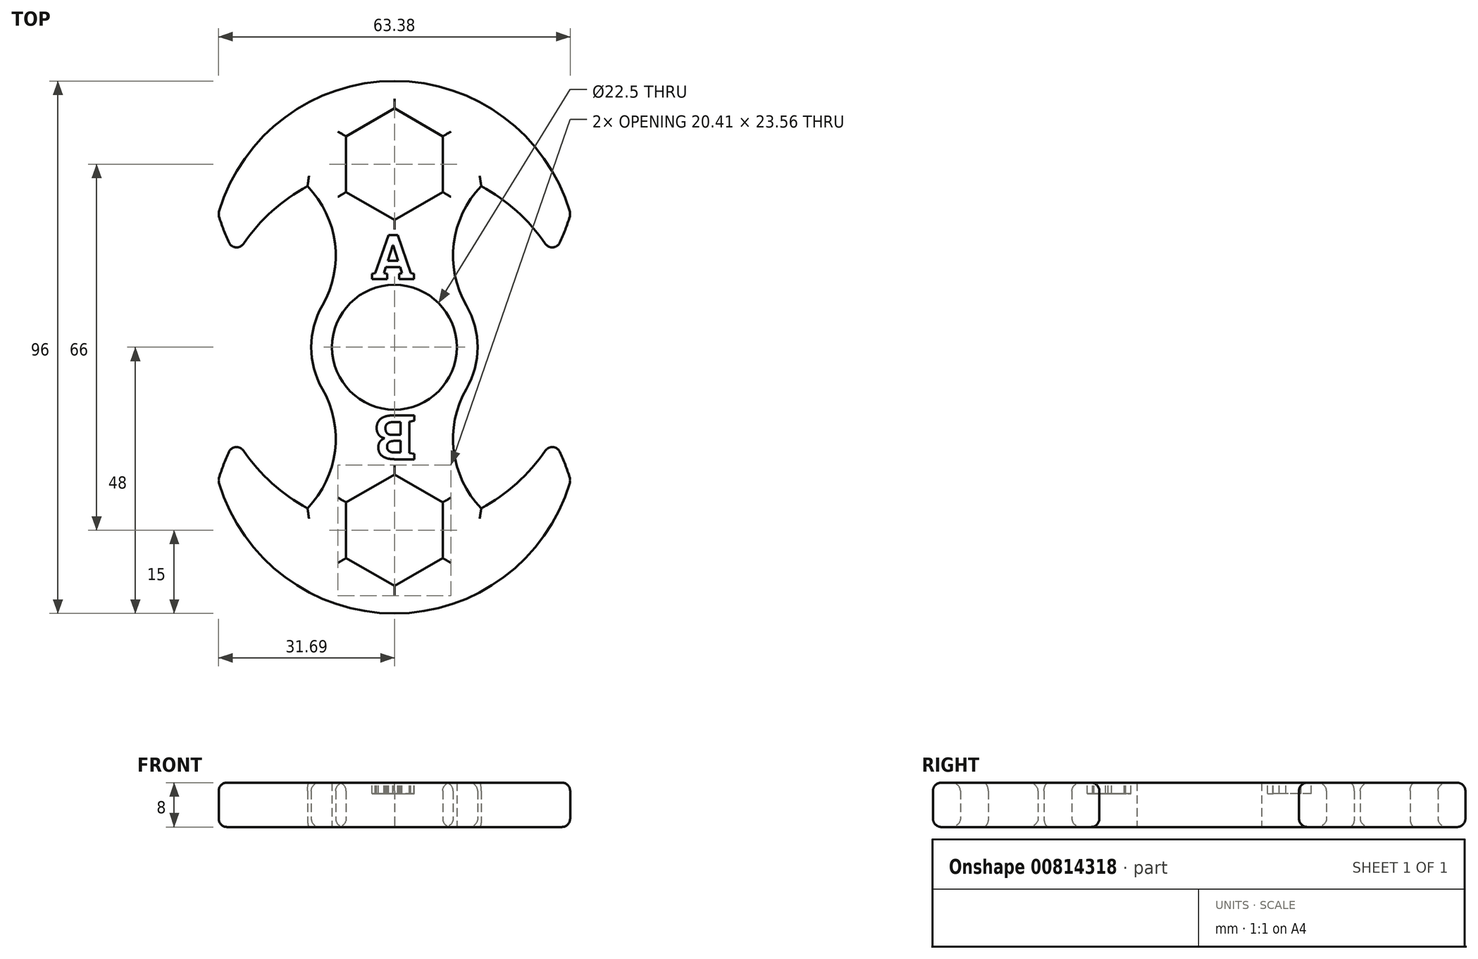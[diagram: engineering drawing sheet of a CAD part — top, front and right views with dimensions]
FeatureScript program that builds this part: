
annotation { "Feature Type Name" : "Feature", "Feature Type Description" : "" }
export const myFeature = defineFeature(function(context is Context, id is Id, definition is map)
    precondition{}
    {
        {
            var Q0;
            Q0=qCreatedBy(makeId("Top.planeOp"),FACE);
            var sketch = newSketch(context, id + "F0", { "sketchPlane" : qUnion([Q0])});
            skCircle(sketch, "E0", {"center": v(0, 0) * mm, "radius": 11.25 * mm});
            skArc(sketch, "E1", {"start": v(13, -7.5) * mm, "mid": v(15, 0) * mm, "end": v(13, 7.5) * mm});
            skCircle(sketch, "E2", {"center": v(0, 33) * mm, "radius": 10.05 * mm});
            skPoint(sketch, "E3.orphan", {"position": v(0, -30.51) * mm});
            skCircle(sketch, "E4", {"center": v(0, -33) * mm, "radius": 10.05 * mm});
            skArc(sketch, "E5", {"start": v(31.75, -24) * mm, "mid": v(30.4, -20.15) * mm, "end": v(28.58, -16.5) * mm});
            skArc(sketch, "E6", {"start": v(28.58, 16.5) * mm, "mid": v(30.4, 20.15) * mm, "end": v(31.75, 24) * mm});
            skArc(sketch, "E7", {"start": v(-28.58, -16.5) * mm, "mid": v(-23, -23.67) * mm, "end": v(-15.67, -29.04) * mm});
            skArc(sketch, "E8", {"start": v(31.75, 24) * mm, "mid": v(0, 48) * mm, "end": v(-31.75, 24) * mm});
            skArc(sketch, "E9", {"start": v(-31.75, -24) * mm, "mid": v(0, -48) * mm, "end": v(31.75, -24) * mm});
            skArc(sketch, "E10.trimOffspring", {"start": v(-28.58, -16.5) * mm, "mid": v(-30.4, -20.15) * mm, "end": v(-31.75, -24) * mm});
            skArc(sketch, "E11.trimOffspring", {"start": v(15.67, -29.04) * mm, "mid": v(23, -23.67) * mm, "end": v(28.58, -16.5) * mm});
            skArc(sketch, "E12.trimOffspring", {"start": v(-31.75, 24) * mm, "mid": v(-30.4, 20.15) * mm, "end": v(-28.58, 16.5) * mm});
            skArc(sketch, "E13.trimOffspring", {"start": v(28.58, 16.5) * mm, "mid": v(23, 23.67) * mm, "end": v(15.67, 29.04) * mm});
            skArc(sketch, "E14", {"start": v(15.67, 29.04) * mm, "mid": v(10.72, 18.72) * mm, "end": v(13, 7.5) * mm});
            skArc(sketch, "E15", {"start": v(13, -7.5) * mm, "mid": v(10.72, -18.72) * mm, "end": v(15.67, -29.04) * mm});
            skArc(sketch, "E16", {"start": v(-15.67, -29.04) * mm, "mid": v(-10.72, -18.72) * mm, "end": v(-13, -7.5) * mm});
            skArc(sketch, "E17.trimOffspring", {"start": v(-13, 7.5) * mm, "mid": v(-10.72, 18.72) * mm, "end": v(-15.67, 29.04) * mm});
            skArc(sketch, "E18.trimOffspring", {"start": v(-15.67, 29.04) * mm, "mid": v(-23, 23.67) * mm, "end": v(-28.58, 16.5) * mm});
            skArc(sketch, "E19.trimOffspring", {"start": v(-13, 7.5) * mm, "mid": v(-15, 0) * mm, "end": v(-13, -7.5) * mm});
            skCircle(sketch, "E20.cCircle", {"center": v(0, 33) * mm, "radius": 10.05 * mm, "construction": true});
            skLineSegment(sketch, "E20.0", {"start": v(0, 22.95) * mm, "end": v(-8.7, 27.98) * mm});
            skLineSegment(sketch, "E20.1", {"start": v(-8.7, 27.98) * mm, "end": v(-8.7, 38.03) * mm});
            skLineSegment(sketch, "E20.2", {"start": v(-8.7, 38.03) * mm, "end": v(0, 43.05) * mm});
            skLineSegment(sketch, "E20.3", {"start": v(0, 43.05) * mm, "end": v(8.7, 38.02) * mm});
            skLineSegment(sketch, "E20.4", {"start": v(8.7, 38.03) * mm, "end": v(8.7, 27.98) * mm});
            skLineSegment(sketch, "E20.5", {"start": v(8.7, 27.98) * mm, "end": v(0, 22.95) * mm});
            skCircle(sketch, "E21.cCircle", {"center": v(0, -33) * mm, "radius": 10.05 * mm, "construction": true});
            skLineSegment(sketch, "E21.0", {"start": v(0, -22.95) * mm, "end": v(8.7, -27.98) * mm});
            skLineSegment(sketch, "E21.1", {"start": v(8.7, -27.98) * mm, "end": v(8.7, -38.03) * mm});
            skLineSegment(sketch, "E21.2", {"start": v(8.7, -38.03) * mm, "end": v(0, -43.05) * mm});
            skLineSegment(sketch, "E21.3", {"start": v(0, -43.05) * mm, "end": v(-8.7, -38.03) * mm});
            skLineSegment(sketch, "E21.4", {"start": v(-8.7, -38.03) * mm, "end": v(-8.7, -27.97) * mm});
            skLineSegment(sketch, "E21.5", {"start": v(-8.7, -27.97) * mm, "end": v(0, -22.95) * mm});
            skSolve(sketch);
        }
        {
            var Q0;
            {var subQ0=sQuery(id+"F0.wireOp",EDGE,"E20.0");Q0=makeQuery(id+"F0.imprint","IMPRINT",FACE,{"disambiguationData":[TD([[makeQuery(id+"F0.imprint","IMPRINT",EDGE,{"derivedFrom":subQ0}),1.0]])]});}
            var Q1;
            {var subQ0=sQuery(id+"F0.wireOp",EDGE,"E20.5");Q1=makeQuery(id+"F0.imprint","IMPRINT",FACE,{"disambiguationData":[TD([[makeQuery(id+"F0.imprint","IMPRINT",EDGE,{"derivedFrom":subQ0}),1.0]])]});}
            var Q2;
            {var subQ0=sQuery(id+"F0.wireOp",EDGE,"E20.4");Q2=makeQuery(id+"F0.imprint","IMPRINT",FACE,{"disambiguationData":[TD([[makeQuery(id+"F0.imprint","IMPRINT",EDGE,{"derivedFrom":subQ0}),1.0]])]});}
            var Q3;
            {var subQ0=sQuery(id+"F0.wireOp",EDGE,"E20.2");Q3=makeQuery(id+"F0.imprint","IMPRINT",FACE,{"disambiguationData":[TD([[makeQuery(id+"F0.imprint","IMPRINT",EDGE,{"derivedFrom":subQ0}),1.0]])]});}
            var Q4;
            {var subQ0=sQuery(id+"F0.wireOp",EDGE,"E20.3");Q4=makeQuery(id+"F0.imprint","IMPRINT",FACE,{"disambiguationData":[TD([[makeQuery(id+"F0.imprint","IMPRINT",EDGE,{"derivedFrom":subQ0}),1.0]])]});}
            var Q5;
            {var subQ0=sQuery(id+"F0.wireOp",EDGE,"E20.1");Q5=makeQuery(id+"F0.imprint","IMPRINT",FACE,{"disambiguationData":[TD([[makeQuery(id+"F0.imprint","IMPRINT",EDGE,{"derivedFrom":subQ0}),1.0]])]});}
            var Q6;
            {var subQ0=sQuery(id+"F0.wireOp",EDGE,"E21.0");Q6=makeQuery(id+"F0.imprint","IMPRINT",FACE,{"disambiguationData":[TD([[makeQuery(id+"F0.imprint","IMPRINT",EDGE,{"derivedFrom":subQ0}),1.0]])]});}
            var Q7;
            {var subQ0=sQuery(id+"F0.wireOp",EDGE,"E21.1");Q7=makeQuery(id+"F0.imprint","IMPRINT",FACE,{"disambiguationData":[TD([[makeQuery(id+"F0.imprint","IMPRINT",EDGE,{"derivedFrom":subQ0}),1.0]])]});}
            var Q8;
            {var subQ0=sQuery(id+"F0.wireOp",EDGE,"E21.2");Q8=makeQuery(id+"F0.imprint","IMPRINT",FACE,{"disambiguationData":[TD([[makeQuery(id+"F0.imprint","IMPRINT",EDGE,{"derivedFrom":subQ0}),1.0]])]});}
            var Q9;
            Q9=makeQuery(id+"F0.imprint","IMPRINT",FACE,{"disambiguationData":[TD([[makeQuery(id+"F0.imprint","IMPRINT",EDGE,{"derivedFrom":sQuery(id+"F0.wireOp",EDGE,"E0")}),-1.0]])]});
            var Q10;
            {var subQ0=sQuery(id+"F0.wireOp",EDGE,"E21.3");Q10=makeQuery(id+"F0.imprint","IMPRINT",FACE,{"disambiguationData":[TD([[makeQuery(id+"F0.imprint","IMPRINT",EDGE,{"derivedFrom":subQ0}),1.0]])]});}
            var Q11;
            {var subQ0=sQuery(id+"F0.wireOp",EDGE,"E21.4");Q11=makeQuery(id+"F0.imprint","IMPRINT",FACE,{"disambiguationData":[TD([[makeQuery(id+"F0.imprint","IMPRINT",EDGE,{"derivedFrom":subQ0}),1.0]])]});}
            var Q12;
            {var subQ0=sQuery(id+"F0.wireOp",EDGE,"E21.5");Q12=makeQuery(id+"F0.imprint","IMPRINT",FACE,{"disambiguationData":[TD([[makeQuery(id+"F0.imprint","IMPRINT",EDGE,{"derivedFrom":subQ0}),1.0]])]});}
            var Q13;
            Q13=makeQuery(id+"F0.imprint","IMPRINT",FACE,{"disambiguationData":[TD([[makeQuery(id+"F0.imprint","IMPRINT",EDGE,{"derivedFrom":sQuery(id+"F0.wireOp",EDGE,"b09e6dd1-dab8-4b64-9b37-ad7a02245aec.sketch_text.stroke-16")}),1.0]])]});
            var Q14;
            Q14=makeQuery(id+"F0.imprint","IMPRINT",FACE,{"disambiguationData":[TD([[makeQuery(id+"F0.imprint","IMPRINT",EDGE,{"derivedFrom":sQuery(id+"F0.wireOp",EDGE,"b09e6dd1-dab8-4b64-9b37-ad7a02245aec.sketch_text.stroke-0")}),-1.0]])]});
            var Q15;
            Q15=makeQuery(id+"F0.imprint","IMPRINT",FACE,{"disambiguationData":[TD([[makeQuery(id+"F0.imprint","IMPRINT",EDGE,{"derivedFrom":sQuery(id+"F0.wireOp",EDGE,"b3a1ebe3-2c7f-47d1-8247-27ddfe72ac5a.sketch_text.stroke-23")}),1.0]])]});
            var Q16;
            Q16=makeQuery(id+"F0.imprint","IMPRINT",FACE,{"disambiguationData":[TD([[makeQuery(id+"F0.imprint","IMPRINT",EDGE,{"derivedFrom":sQuery(id+"F0.wireOp",EDGE,"b3a1ebe3-2c7f-47d1-8247-27ddfe72ac5a.sketch_text.stroke-16")}),1.0]])]});
            var Q17;
            Q17=makeQuery(id+"F0.imprint","IMPRINT",FACE,{"disambiguationData":[TD([[makeQuery(id+"F0.imprint","IMPRINT",EDGE,{"derivedFrom":sQuery(id+"F0.wireOp",EDGE,"b3a1ebe3-2c7f-47d1-8247-27ddfe72ac5a.sketch_text.stroke-0")}),-1.0]])]});
            extrude(context, id + "F1", {"entities" : qUnion([Q0, Q1, Q2, Q3, Q4, Q5, Q6, Q7, Q8, Q9, Q10, Q11, Q12, Q13, Q14, Q15, Q16, Q17]), "depth" : 8 * mm, "offsetDistance" : 25 * mm});
        }
        {
            var Q0;
            Q0=makeQuery(id+"F1.opExtrude","CAP_EDGE",EDGE,{"disambiguationData":[OSD([sQuery(id+"F0.wireOp",EDGE,"E8")])],"isStart":false});
            var Q1;
            Q1=makeQuery(id+"F1.opExtrude","CAP_EDGE",EDGE,{"disambiguationData":[OSD([sQuery(id+"F0.wireOp",EDGE,"E12.trimOffspring")])],"isStart":false});
            var Q2;
            Q2=makeQuery(id+"F1.opExtrude","CAP_EDGE",EDGE,{"disambiguationData":[OSD([sQuery(id+"F0.wireOp",EDGE,"E18.trimOffspring")])],"isStart":false});
            var Q3;
            Q3=makeQuery(id+"F1.opExtrude","CAP_EDGE",EDGE,{"disambiguationData":[OSD([sQuery(id+"F0.wireOp",EDGE,"E17.trimOffspring")])],"isStart":false});
            var Q4;
            Q4=makeQuery(id+"F1.opExtrude","CAP_EDGE",EDGE,{"disambiguationData":[OSD([sQuery(id+"F0.wireOp",EDGE,"E15")])],"isStart":false});
            var Q5;
            Q5=makeQuery(id+"F1.opExtrude","CAP_EDGE",EDGE,{"disambiguationData":[OSD([sQuery(id+"F0.wireOp",EDGE,"E13.trimOffspring")])],"isStart":false});
            var Q6;
            Q6=makeQuery(id+"F1.opExtrude","CAP_EDGE",EDGE,{"disambiguationData":[OSD([sQuery(id+"F0.wireOp",EDGE,"E6")])],"isStart":false});
            var Q7;
            Q7=makeQuery(id+"F1.opExtrude","CAP_EDGE",EDGE,{"disambiguationData":[OSD([sQuery(id+"F0.wireOp",EDGE,"E9")])],"isStart":false});
            var Q8;
            Q8=makeQuery(id+"F1.opExtrude","CAP_EDGE",EDGE,{"disambiguationData":[OSD([sQuery(id+"F0.wireOp",EDGE,"E5")])],"isStart":false});
            var Q9;
            Q9=makeQuery(id+"F1.opExtrude","CAP_EDGE",EDGE,{"disambiguationData":[OSD([sQuery(id+"F0.wireOp",EDGE,"E7")])],"isStart":false});
            var Q10;
            Q10=makeQuery(id+"F1.opExtrude","CAP_EDGE",EDGE,{"disambiguationData":[OSD([sQuery(id+"F0.wireOp",EDGE,"E10.trimOffspring")])],"isStart":false});
            var Q11;
            Q11=makeQuery(id+"F1.opExtrude","CAP_EDGE",EDGE,{"disambiguationData":[OSD([sQuery(id+"F0.wireOp",EDGE,"E11.trimOffspring")])],"isStart":false});
            var Q12;
            Q12=makeQuery(id+"F1.opExtrude","CAP_EDGE",EDGE,{"disambiguationData":[OSD([sQuery(id+"F0.wireOp",EDGE,"E9")])],"isStart":true});
            var Q13;
            Q13=makeQuery(id+"F1.opExtrude","CAP_EDGE",EDGE,{"disambiguationData":[OSD([sQuery(id+"F0.wireOp",EDGE,"E5")])],"isStart":true});
            var Q14;
            Q14=makeQuery(id+"F1.opExtrude","CAP_EDGE",EDGE,{"disambiguationData":[OSD([sQuery(id+"F0.wireOp",EDGE,"E11.trimOffspring")])],"isStart":true});
            var Q15;
            Q15=makeQuery(id+"F1.opExtrude","CAP_EDGE",EDGE,{"disambiguationData":[OSD([sQuery(id+"F0.wireOp",EDGE,"E15")])],"isStart":true});
            var Q16;
            Q16=makeQuery(id+"F1.opExtrude","CAP_EDGE",EDGE,{"disambiguationData":[OSD([sQuery(id+"F0.wireOp",EDGE,"E13.trimOffspring")])],"isStart":true});
            var Q17;
            Q17=makeQuery(id+"F1.opExtrude","CAP_EDGE",EDGE,{"disambiguationData":[OSD([sQuery(id+"F0.wireOp",EDGE,"E8")])],"isStart":true});
            var Q18;
            Q18=makeQuery(id+"F1.opExtrude","CAP_EDGE",EDGE,{"disambiguationData":[OSD([sQuery(id+"F0.wireOp",EDGE,"E12.trimOffspring")])],"isStart":true});
            var Q19;
            Q19=makeQuery(id+"F1.opExtrude","CAP_EDGE",EDGE,{"disambiguationData":[OSD([sQuery(id+"F0.wireOp",EDGE,"E17.trimOffspring")])],"isStart":true});
            var Q20;
            Q20=makeQuery(id+"F1.opExtrude","CAP_EDGE",EDGE,{"disambiguationData":[OSD([sQuery(id+"F0.wireOp",EDGE,"E10.trimOffspring")])],"isStart":true});
            var Q21;
            Q21=makeQuery(id+"F1.opExtrude","CAP_EDGE",EDGE,{"disambiguationData":[OSD([sQuery(id+"F0.wireOp",EDGE,"E7")])],"isStart":true});
            var Q22;
            Q22=makeQuery(id+"F1.opExtrude","CAP_EDGE",EDGE,{"disambiguationData":[OSD([sQuery(id+"F0.wireOp",EDGE,"E18.trimOffspring")])],"isStart":true});
            var Q23;
            Q23=makeQuery(id+"F1.opExtrude","SWEPT_EDGE",EDGE,{"disambiguationData":[OSD([sQuery(id+"F0.wireOp",EDGE,"E12.trimOffspring"),sQuery(id+"F0.wireOp",EDGE,"E18.trimOffspring")])]});
            var Q24;
            Q24=makeQuery(id+"F1.opExtrude","SWEPT_EDGE",EDGE,{"disambiguationData":[OSD([sQuery(id+"F0.wireOp",EDGE,"E6"),sQuery(id+"F0.wireOp",EDGE,"E13.trimOffspring")])]});
            var Q25;
            Q25=makeQuery(id+"F1.opExtrude","CAP_EDGE",EDGE,{"disambiguationData":[OSD([sQuery(id+"F0.wireOp",EDGE,"E6")])],"isStart":true});
            var Q26;
            Q26=makeQuery(id+"F1.opExtrude","SWEPT_EDGE",EDGE,{"disambiguationData":[OSD([sQuery(id+"F0.wireOp",EDGE,"E5"),sQuery(id+"F0.wireOp",EDGE,"E9")])]});
            var Q27;
            Q27=makeQuery(id+"F1.opExtrude","SWEPT_EDGE",EDGE,{"disambiguationData":[OSD([sQuery(id+"F0.wireOp",EDGE,"E5"),sQuery(id+"F0.wireOp",EDGE,"E11.trimOffspring")])]});
            var Q28;
            Q28=makeQuery(id+"F1.opExtrude","SWEPT_EDGE",EDGE,{"disambiguationData":[OSD([sQuery(id+"F0.wireOp",EDGE,"E6"),sQuery(id+"F0.wireOp",EDGE,"E8")])]});
            var Q29;
            Q29=makeQuery(id+"F1.opExtrude","SWEPT_EDGE",EDGE,{"disambiguationData":[OSD([sQuery(id+"F0.wireOp",EDGE,"E8"),sQuery(id+"F0.wireOp",EDGE,"E12.trimOffspring")])]});
            var Q30;
            Q30=makeQuery(id+"F1.opExtrude","SWEPT_EDGE",EDGE,{"disambiguationData":[OSD([sQuery(id+"F0.wireOp",EDGE,"E7"),sQuery(id+"F0.wireOp",EDGE,"E10.trimOffspring")])]});
            var Q31;
            Q31=makeQuery(id+"F1.opExtrude","SWEPT_EDGE",EDGE,{"disambiguationData":[OSD([sQuery(id+"F0.wireOp",EDGE,"E9"),sQuery(id+"F0.wireOp",EDGE,"E10.trimOffspring")])]});
            var Q32;
            Q32=makeQuery(id+"F1.opExtrude","CAP_EDGE",EDGE,{"disambiguationData":[OSD([sQuery(id+"F0.wireOp",EDGE,"E20.1")])],"isStart":false});
            var Q33;
            Q33=makeQuery(id+"F1.opExtrude","CAP_EDGE",EDGE,{"disambiguationData":[OSD([sQuery(id+"F0.wireOp",EDGE,"E20.2")])],"isStart":false});
            var Q34;
            Q34=makeQuery(id+"F1.opExtrude","CAP_EDGE",EDGE,{"disambiguationData":[OSD([sQuery(id+"F0.wireOp",EDGE,"E20.3")])],"isStart":false});
            var Q35;
            Q35=makeQuery(id+"F1.opExtrude","CAP_EDGE",EDGE,{"disambiguationData":[OSD([sQuery(id+"F0.wireOp",EDGE,"E20.4")])],"isStart":false});
            var Q36;
            Q36=makeQuery(id+"F1.opExtrude","CAP_EDGE",EDGE,{"disambiguationData":[OSD([sQuery(id+"F0.wireOp",EDGE,"E20.5")])],"isStart":false});
            var Q37;
            Q37=makeQuery(id+"F1.opExtrude","CAP_EDGE",EDGE,{"disambiguationData":[OSD([sQuery(id+"F0.wireOp",EDGE,"E21.5")])],"isStart":false});
            var Q38;
            Q38=makeQuery(id+"F1.opExtrude","CAP_EDGE",EDGE,{"disambiguationData":[OSD([sQuery(id+"F0.wireOp",EDGE,"E21.0")])],"isStart":false});
            var Q39;
            Q39=makeQuery(id+"F1.opExtrude","CAP_EDGE",EDGE,{"disambiguationData":[OSD([sQuery(id+"F0.wireOp",EDGE,"E21.4")])],"isStart":false});
            var Q40;
            Q40=makeQuery(id+"F1.opExtrude","CAP_EDGE",EDGE,{"disambiguationData":[OSD([sQuery(id+"F0.wireOp",EDGE,"E21.3")])],"isStart":false});
            var Q41;
            Q41=makeQuery(id+"F1.opExtrude","CAP_EDGE",EDGE,{"disambiguationData":[OSD([sQuery(id+"F0.wireOp",EDGE,"E21.2")])],"isStart":false});
            var Q42;
            Q42=makeQuery(id+"F1.opExtrude","CAP_EDGE",EDGE,{"disambiguationData":[OSD([sQuery(id+"F0.wireOp",EDGE,"E21.1")])],"isStart":false});
            var Q43;
            Q43=makeQuery(id+"F1.opExtrude","CAP_EDGE",EDGE,{"disambiguationData":[OSD([sQuery(id+"F0.wireOp",EDGE,"E21.4")])],"isStart":true});
            var Q44;
            Q44=makeQuery(id+"F1.opExtrude","CAP_EDGE",EDGE,{"disambiguationData":[OSD([sQuery(id+"F0.wireOp",EDGE,"E21.3")])],"isStart":true});
            var Q45;
            Q45=makeQuery(id+"F1.opExtrude","CAP_EDGE",EDGE,{"disambiguationData":[OSD([sQuery(id+"F0.wireOp",EDGE,"E21.2")])],"isStart":true});
            var Q46;
            Q46=makeQuery(id+"F1.opExtrude","CAP_EDGE",EDGE,{"disambiguationData":[OSD([sQuery(id+"F0.wireOp",EDGE,"E21.1")])],"isStart":true});
            var Q47;
            Q47=makeQuery(id+"F1.opExtrude","CAP_EDGE",EDGE,{"disambiguationData":[OSD([sQuery(id+"F0.wireOp",EDGE,"E21.0")])],"isStart":true});
            var Q48;
            Q48=makeQuery(id+"F1.opExtrude","CAP_EDGE",EDGE,{"disambiguationData":[OSD([sQuery(id+"F0.wireOp",EDGE,"E21.5")])],"isStart":true});
            var Q49;
            Q49=makeQuery(id+"F1.opExtrude","CAP_EDGE",EDGE,{"disambiguationData":[OSD([sQuery(id+"F0.wireOp",EDGE,"E20.5")])],"isStart":true});
            var Q50;
            Q50=makeQuery(id+"F1.opExtrude","CAP_EDGE",EDGE,{"disambiguationData":[OSD([sQuery(id+"F0.wireOp",EDGE,"E20.2")])],"isStart":true});
            var Q51;
            Q51=makeQuery(id+"F1.opExtrude","CAP_EDGE",EDGE,{"disambiguationData":[OSD([sQuery(id+"F0.wireOp",EDGE,"E20.3")])],"isStart":true});
            var Q52;
            Q52=makeQuery(id+"F1.opExtrude","CAP_EDGE",EDGE,{"disambiguationData":[OSD([sQuery(id+"F0.wireOp",EDGE,"E20.0")])],"isStart":true});
            var Q53;
            Q53=makeQuery(id+"F1.opExtrude","CAP_EDGE",EDGE,{"disambiguationData":[OSD([sQuery(id+"F0.wireOp",EDGE,"E20.4")])],"isStart":true});
            var Q54;
            Q54=makeQuery(id+"F1.opExtrude","CAP_EDGE",EDGE,{"disambiguationData":[OSD([sQuery(id+"F0.wireOp",EDGE,"E20.1")])],"isStart":true});
            var Q55;
            Q55=makeQuery(id+"F1.opExtrude","CAP_EDGE",EDGE,{"disambiguationData":[OSD([sQuery(id+"F0.wireOp",EDGE,"E20.0")])],"isStart":false});
            fillet(context, id + "F2", {"entities" : qUnion([Q0, Q1, Q2, Q3, Q4, Q5, Q6, Q7, Q8, Q9, Q10, Q11, Q12, Q13, Q14, Q15, Q16, Q17, Q18, Q19, Q20, Q21, Q22, Q23, Q24, Q25, Q26, Q27, Q28, Q29, Q30, Q31, Q32, Q33, Q34, Q35, Q36, Q37, Q38, Q39, Q40, Q41, Q42, Q43, Q44, Q45, Q46, Q47, Q48, Q49, Q50, Q51, Q52, Q53, Q54, Q55]), "radius" : 1.5 * mm, "tangentPropagation" : true, "allowEdgeOverflow" : false});
        }
        {
            var Q0;
            Q0=makeQuery(id+"F1.opExtrude","CAP_FACE",FACE,{"disambiguationData":[OSD([sQuery(id+"F0.wireOp",EDGE,"E0"),sQuery(id+"F0.wireOp",EDGE,"E1"),sQuery(id+"F0.wireOp",EDGE,"E5"),sQuery(id+"F0.wireOp",EDGE,"E6"),sQuery(id+"F0.wireOp",EDGE,"E7"),sQuery(id+"F0.wireOp",EDGE,"E8"),sQuery(id+"F0.wireOp",EDGE,"E9"),sQuery(id+"F0.wireOp",EDGE,"E10.trimOffspring"),sQuery(id+"F0.wireOp",EDGE,"E11.trimOffspring"),sQuery(id+"F0.wireOp",EDGE,"E12.trimOffspring"),sQuery(id+"F0.wireOp",EDGE,"E13.trimOffspring"),sQuery(id+"F0.wireOp",EDGE,"E14"),sQuery(id+"F0.wireOp",EDGE,"E15"),sQuery(id+"F0.wireOp",EDGE,"E16"),sQuery(id+"F0.wireOp",EDGE,"E17.trimOffspring"),sQuery(id+"F0.wireOp",EDGE,"E18.trimOffspring"),sQuery(id+"F0.wireOp",EDGE,"E19.trimOffspring"),sQuery(id+"F0.wireOp",EDGE,"E20.0"),sQuery(id+"F0.wireOp",EDGE,"E20.1"),sQuery(id+"F0.wireOp",EDGE,"E20.2"),sQuery(id+"F0.wireOp",EDGE,"E20.3"),sQuery(id+"F0.wireOp",EDGE,"E20.4"),sQuery(id+"F0.wireOp",EDGE,"E20.5"),sQuery(id+"F0.wireOp",EDGE,"E21.0"),sQuery(id+"F0.wireOp",EDGE,"E21.1"),sQuery(id+"F0.wireOp",EDGE,"E21.2"),sQuery(id+"F0.wireOp",EDGE,"E21.3"),sQuery(id+"F0.wireOp",EDGE,"E21.4"),sQuery(id+"F0.wireOp",EDGE,"E21.5")])],"isStart":false});
            var sketch = newSketch(context, id + "F3", { "sketchPlane" : qUnion([Q0])});
            skText(sketch, "E22", { "text": "A", "fontName": "RobotoSlab-Bold.ttf"});
            skText(sketch, "E23", { "text": "B", "fontName": "RobotoSlab-Bold.ttf"});
            const initialGuessF3  = {"E22": [-0.00424, 0.01231, 1, 0, 0.008], "E23": [0.00386, -0.0123, -1, 0, 0.008]};
            skSetInitialGuess(sketch, initialGuessF3);
            skSolve(sketch);
        }
        {
            var Q0;
            Q0=makeQuery(id+"F3.imprint","IMPRINT",FACE,{"disambiguationData":[TD([[makeQuery(id+"F3.imprint","IMPRINT",EDGE,{"derivedFrom":sQuery(id+"F3.wireOp",EDGE,"E23.sketch_text.stroke-0")}),-1.0]])]});
            var Q1;
            Q1=makeQuery(id+"F3.imprint","IMPRINT",FACE,{"disambiguationData":[TD([[makeQuery(id+"F3.imprint","IMPRINT",EDGE,{"derivedFrom":sQuery(id+"F3.wireOp",EDGE,"E22.sketch_text.stroke-0")}),-1.0]])]});
            var Q2;
            Q2 = qConstructionFilter(qBodyType(qCreatedBy(id + "F3" ,EDGE), BodyType.WIRE), ConstructionObject.NO);
            extrude(context, id + "F4", {"entities" : qUnion([Q0, Q1]), "operationType" : NewBodyOperationType.REMOVE, "surfaceEntities" : qUnion([Q2]), "oppositeDirection" : true, "depth" : 2 * mm, "offsetDistance" : 25 * mm});
        }
    });
